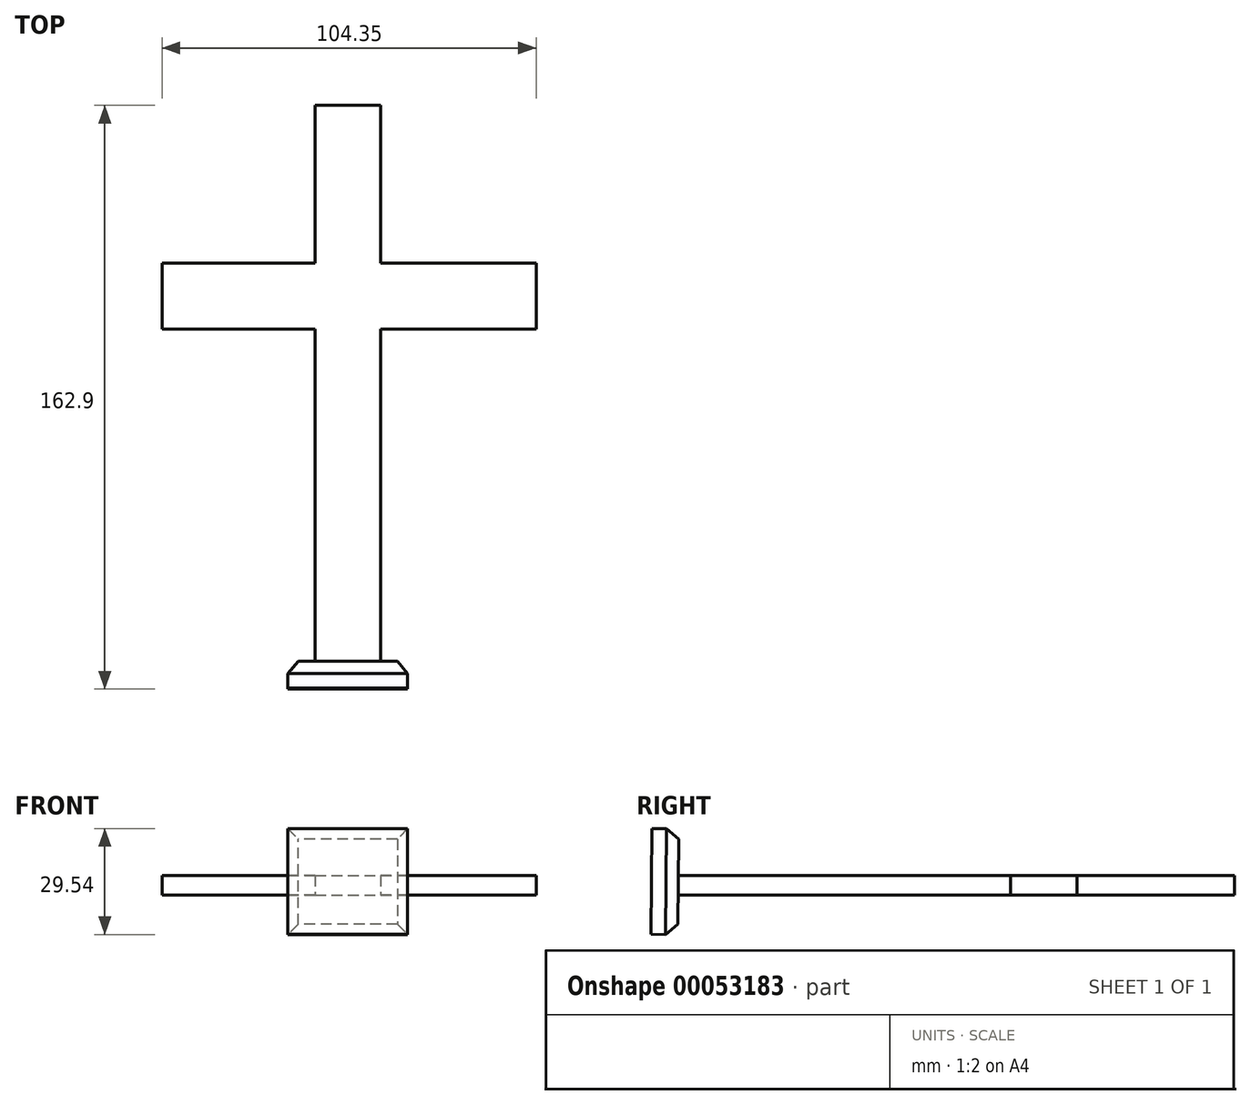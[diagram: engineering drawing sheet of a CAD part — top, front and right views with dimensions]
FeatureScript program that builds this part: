
annotation { "Feature Type Name" : "Feature", "Feature Type Description" : "" }
export const myFeature = defineFeature(function(context is Context, id is Id, definition is map)
    precondition{}
    {
        {
            var Q0;
            Q0=qCreatedBy(makeId("Top.planeOp"),FACE);
            var sketch = newSketch(context, id + "F0", { "sketchPlane" : qUnion([Q0])});
            skLineSegment(sketch, "E0", {"start": v(0, 81.3) * mm, "end": v(9.15, 81.3) * mm});
            skLineSegment(sketch, "E1", {"start": v(9.15, 81.3) * mm, "end": v(9.15, 37.3) * mm});
            skLineSegment(sketch, "E2", {"start": v(9.15, 37.3) * mm, "end": v(52.55, 37.3) * mm});
            skLineSegment(sketch, "E3", {"start": v(52.55, 37.3) * mm, "end": v(52.55, 18.8) * mm});
            skLineSegment(sketch, "E4", {"start": v(52.55, 18.8) * mm, "end": v(9.15, 18.8) * mm});
            skLineSegment(sketch, "E5", {"start": v(9.15, 18.8) * mm, "end": v(9.15, -81.2) * mm});
            skLineSegment(sketch, "E6", {"start": v(9.15, -81.2) * mm, "end": v(0, -81.2) * mm});
            skLineSegment(sketch, "E7", {"start": v(0, 0) * mm, "end": v(0, 81.3) * mm, "construction": true});
            skLineSegment(sketch, "E8", {"start": v(0, 0) * mm, "end": v(0, -81.2) * mm, "construction": true});
            skLineSegment(sketch, "E9.MirrorCS", {"start": v(0, 81.3) * mm, "end": v(-9.15, 81.3) * mm});
            skLineSegment(sketch, "E10.MirrorCS", {"start": v(-9.15, 81.3) * mm, "end": v(-9.15, 37.3) * mm});
            skLineSegment(sketch, "E11.MirrorCS", {"start": v(-9.15, 37.3) * mm, "end": v(-51.8, 37.3) * mm});
            skLineSegment(sketch, "E12.MirrorCS", {"start": v(-51.8, 18.8) * mm, "end": v(-9.15, 18.8) * mm});
            skLineSegment(sketch, "E13.MirrorCS", {"start": v(-9.15, 18.8) * mm, "end": v(-9.15, -81.2) * mm});
            skLineSegment(sketch, "E14.MirrorCS", {"start": v(-9.15, -81.2) * mm, "end": v(0, -81.2) * mm});
            skLineSegment(sketch, "E15", {"start": v(-51.8, 37.3) * mm, "end": v(-51.8, 18.8) * mm});
            skPoint(sketch, "E16.orphan", {"position": v(-52.55, 37.3) * mm});
            skPoint(sketch, "E17.MirrorCS.end.orphan", {"position": v(-52.55, 18.8) * mm});
            skSolve(sketch);
        }
        {
            var Q0;
            Q0=makeQuery(id+"F0.imprint","IMPRINT",FACE,{"disambiguationData":[TD([[makeQuery(id+"F0.imprint","IMPRINT",EDGE,{"derivedFrom":sQuery(id+"F0.wireOp",EDGE,"E0")}),-1.0]])]});
            extrude(context, id + "F1", {"entities" : qUnion([Q0]), "endBound" : BoundingType.SYMMETRIC, "depth" : 5.5 * mm});
        }
        {
            var Q0;
            Q0=qCreatedBy(makeId("Right.planeOp"),FACE);
            var sketch = newSketch(context, id + "F2", { "sketchPlane" : qUnion([Q0])});
            skLineSegment(sketch, "E18", {"start": v(-74, -2.75) * mm, "end": v(-74, -34.46) * mm, "construction": true});
            skLineSegment(sketch, "E19", {"start": v(-74, -2.75) * mm, "end": v(18.8, -2.75) * mm, "construction": true});
            skLineSegment(sketch, "E20", {"start": v(-74, -2.75) * mm, "end": v(81.3, -4.15) * mm, "construction": true});
            skLineSegment(sketch, "E21", {"start": v(81.3, -2.73) * mm, "end": v(81.3, -4.15) * mm, "construction": true});
            skLineSegment(sketch, "E22", {"start": v(84.6, 2.75) * mm, "end": v(105.85, 2.75) * mm, "construction": true});
            skLineSegment(sketch, "E23", {"start": v(-74, -2.75) * mm, "end": v(-73.86, 12.9) * mm});
            skLineSegment(sketch, "E24", {"start": v(-73.86, 12.9) * mm, "end": v(-77.23, 15.78) * mm});
            skLineSegment(sketch, "E25", {"start": v(-74, -2.75) * mm, "end": v(-81.5, -2.68) * mm, "construction": true});
            skLineSegment(sketch, "E26", {"start": v(-81.5, -2.68) * mm, "end": v(-81.33, 15.82) * mm});
            skLineSegment(sketch, "E27", {"start": v(-81.33, 15.82) * mm, "end": v(-77.23, 15.78) * mm});
            skLineSegment(sketch, "E28", {"start": v(-81.5, -2.68) * mm, "end": v(-81.6, -13.68) * mm});
            skPoint(sketch, "E29", {"position": v(-74, -18.6) * mm});
            skLineSegment(sketch, "E30", {"start": v(-74, -2.75) * mm, "end": v(-74, -2.75) * mm});
            skLineSegment(sketch, "E31", {"start": v(-81.6, -13.68) * mm, "end": v(-77.5, -13.72) * mm});
            skPoint(sketch, "E32", {"position": v(-74, -2.75) * mm});
            skLineSegment(sketch, "E33", {"start": v(-74, -2.75) * mm, "end": v(-74.07, -10.9) * mm});
            skLineSegment(sketch, "E34", {"start": v(-77.5, -13.72) * mm, "end": v(-74.07, -10.9) * mm});
            skSolve(sketch);
        }
        {
            var Q0;
            Q0 = qSketchRegion(id + "F2", true);
            extrude(context, id + "F3", {"entities" : qUnion([Q0]), "operationType" : NewBodyOperationType.ADD, "endBound" : BoundingType.SYMMETRIC, "depth" : 33.4 * mm});
        }
        {
            var Q0;
            Q0=makeQuery(id+"F3.opExtrude","CAP_EDGE",EDGE,{"disambiguationData":[OSD([sQuery(id+"F2.wireOp",EDGE,"E23"),sQuery(id+"F2.wireOp",EDGE,"E33")])],"isStart":false});
            var Q1;
            Q1=makeQuery(id+"F3.opExtrude","CAP_EDGE",EDGE,{"disambiguationData":[OSD([sQuery(id+"F2.wireOp",EDGE,"E23"),sQuery(id+"F2.wireOp",EDGE,"E33")])],"isStart":true});
            chamfer(context, id + "F4", {"entities" : qUnion([Q0, Q1]), "chamferType" : ChamferType.OFFSET_ANGLE, "width" : 3.4 * mm, "oppositeDirection" : false, "angle" : 40 * degree, "tangentPropagation" : true});
        }
    });
